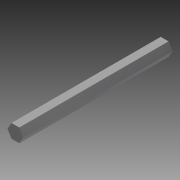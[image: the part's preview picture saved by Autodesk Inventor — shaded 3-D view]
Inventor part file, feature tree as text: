
AUTODESK INVENTOR PART (.ipt)
format: ipt  version: 2014 (Build 180170000, 170)  size: 91,648 bytes
history: native  units: in
note: dims shown in document units (in); Inventor stores cm internally (conversion verified against a paired STEP export)
features: extrude x1, sketch x1
ambient origin geometry x8: Origin, YZ Plane, XZ Plane, XY Plane, X Axis, Y Axis, Z Axis, Center Point
bodies: Solid1 (feature_tree)
feature tree (2):
  extrude  "Extrusion1"  Depth=5.5in TaperAngle=0.0deg
  sketch  "Sketch1"  dims[d0=0.5in d1=5.5in d2=0.0in]
